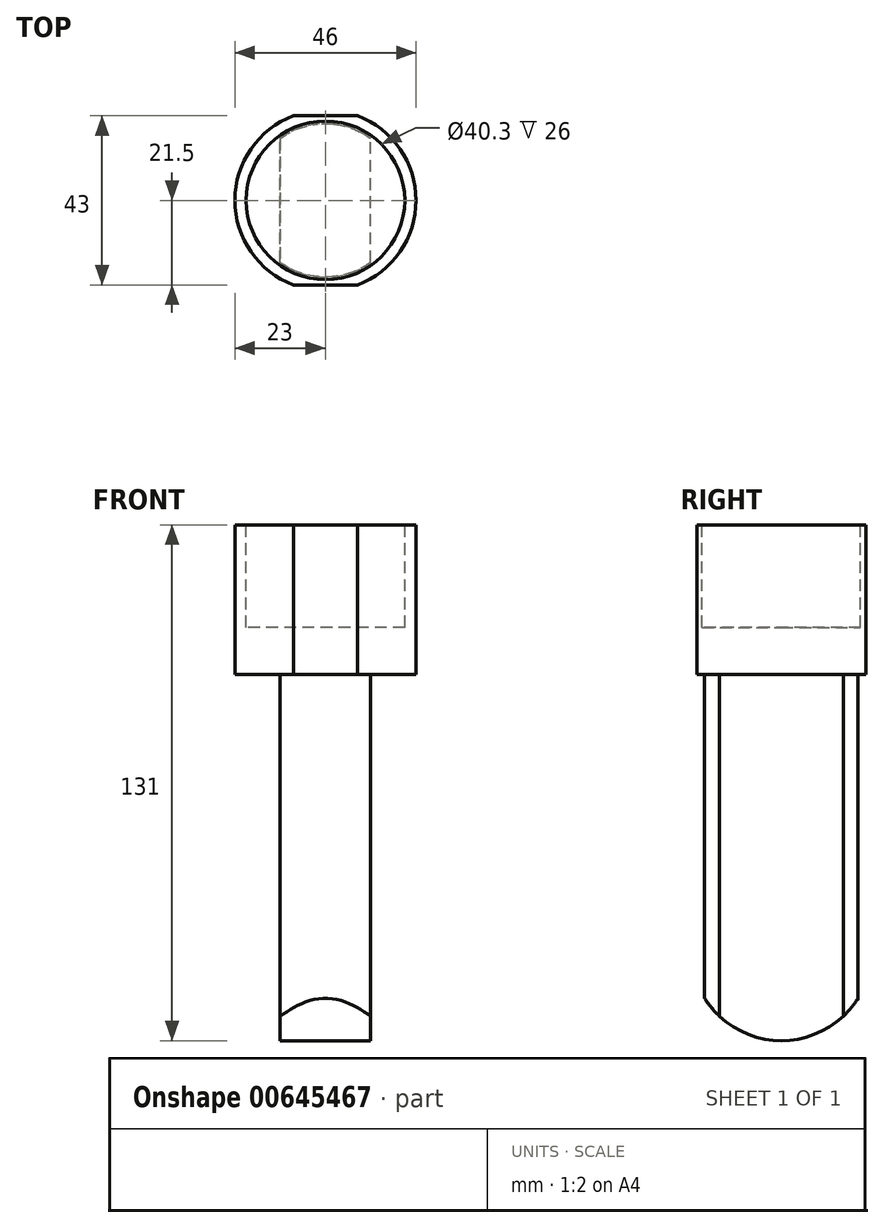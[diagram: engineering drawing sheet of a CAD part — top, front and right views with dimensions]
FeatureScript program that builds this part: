
annotation { "Feature Type Name" : "Feature", "Feature Type Description" : "" }
export const myFeature = defineFeature(function(context is Context, id is Id, definition is map)
    precondition{}
    {
        {
            var Q0;
            Q0=qCreatedBy(makeId("Top.planeOp"),FACE);
            var sketch = newSketch(context, id + "F0", { "sketchPlane" : qUnion([Q0])});
            skArc(sketch, "E0", {"start": v(8.17, -21.5) * mm, "mid": v(23, 0) * mm, "end": v(8.17, 21.5) * mm});
            skLineSegment(sketch, "E1", {"start": v(-8.17, -21.5) * mm, "end": v(8.17, -21.5) * mm});
            skLineSegment(sketch, "E2.MirrorCS", {"start": v(-8.17, 21.5) * mm, "end": v(8.17, 21.5) * mm});
            skArc(sketch, "E3.trimOffspring", {"start": v(-8.17, 21.5) * mm, "mid": v(-23, 0) * mm, "end": v(-8.17, -21.5) * mm});
            skSolve(sketch);
        }
        {
            var Q0;
            Q0 = qSketchRegion(id + "F0", true);
            extrude(context, id + "F1", {"entities" : qUnion([Q0]), "depth" : 38 * mm, "offsetDistance" : 25 * mm});
        }
        {
            var Q0;
            Q0=makeQuery(id+"F1.opExtrude","CAP_FACE",FACE,{"disambiguationData":[OSD([sQuery(id+"F0.wireOp",EDGE,"E0"),sQuery(id+"F0.wireOp",EDGE,"E1"),sQuery(id+"F0.wireOp",EDGE,"E2.MirrorCS"),sQuery(id+"F0.wireOp",EDGE,"E3.trimOffspring")])],"isStart":false});
            var sketch = newSketch(context, id + "F2", { "sketchPlane" : qUnion([Q0])});
            skCircle(sketch, "E4", {"center": v(0, 0) * mm, "radius": 20.15 * mm});
            skSolve(sketch);
        }
        {
            var Q0;
            Q0 = qSketchRegion(id + "F2", true);
            extrude(context, id + "F3", {"entities" : qUnion([Q0]), "operationType" : NewBodyOperationType.REMOVE, "oppositeDirection" : true, "depth" : 26 * mm, "offsetDistance" : 25 * mm});
        }
        {
            var Q0;
            Q0=makeQuery(id+"F1.opExtrude","CAP_FACE",FACE,{"disambiguationData":[OSD([sQuery(id+"F0.wireOp",EDGE,"E0"),sQuery(id+"F0.wireOp",EDGE,"E1"),sQuery(id+"F0.wireOp",EDGE,"E2.MirrorCS"),sQuery(id+"F0.wireOp",EDGE,"E3.trimOffspring")])],"isStart":true});
            var sketch = newSketch(context, id + "F4", { "sketchPlane" : qUnion([Q0])});
            skArc(sketch, "E5", {"start": v(-11.5, -15.75) * mm, "mid": v(0, -19.5) * mm, "end": v(11.5, -15.75) * mm});
            skLineSegment(sketch, "E6", {"start": v(-11.5, 15.75) * mm, "end": v(-11.5, -15.75) * mm});
            skLineSegment(sketch, "E7.MirrorCS", {"start": v(11.5, 15.75) * mm, "end": v(11.5, -15.75) * mm});
            skArc(sketch, "E8.trimOffspring", {"start": v(11.5, 15.75) * mm, "mid": v(0, 19.5) * mm, "end": v(-11.5, 15.75) * mm});
            skSolve(sketch);
        }
        {
            var Q0;
            Q0=makeQuery(id+"F4.imprint","IMPRINT",FACE,{"disambiguationData":[TD([[makeQuery(id+"F4.imprint","IMPRINT",EDGE,{"derivedFrom":sQuery(id+"F4.wireOp",EDGE,"E5")}),1.0]])]});
            extrude(context, id + "F5", {"entities" : qUnion([Q0]), "operationType" : NewBodyOperationType.ADD, "depth" : 93 * mm, "offsetDistance" : 25 * mm});
        }
        {
            var Q0;
            Q0=makeQuery(id+"F5.opExtrude","SWEPT_FACE",FACE,{"disambiguationData":[OSD([sQuery(id+"F4.wireOp",EDGE,"E6")])]});
            var sketch = newSketch(context, id + "F6", { "sketchPlane" : qUnion([Q0])});
            skCircle(sketch, "E9", {"center": v(0, -70) * mm, "radius": 23 * mm});
            skLineSegment(sketch, "E10", {"start": v(-19.4, -82.36) * mm, "end": v(-29.57, -99.34) * mm});
            skLineSegment(sketch, "E11", {"start": v(-29.57, -99.34) * mm, "end": v(32.34, -99.34) * mm});
            skLineSegment(sketch, "E12", {"start": v(32.34, -99.34) * mm, "end": v(19.7, -81.88) * mm});
            skSolve(sketch);
        }
        {
            var Q0;
            {var subQ5=sQuery(id+"F6.wireOp",EDGE,"E10");Q0=makeQuery(id+"F6.imprint","IMPRINT",FACE,{"disambiguationData":[TD([[makeQuery(id+"F6.imprint","IMPRINT",EDGE,{"derivedFrom":subQ5}),1.0]])]});}
            var Q1;
            {var subQ0=sQuery(id+"F6.wireOp",EDGE,"E9");var subQ1=sQuery(id+"F4.wireOp",EDGE,"E6");var subQ4=makeQuery(id+"F5.opExtrude","CAP_EDGE",EDGE,{"disambiguationData":[OSD([subQ1])],"isStart":false});var subQ5=makeQuery(id+"F6.imprint","INTERSECT",VERTEX,{"derivedFrom":[subQ4,subQ0]});Q1=makeQuery(id+"F6.imprint","IMPRINT",FACE,{"disambiguationData":[TD([[makeQuery(id+"F6.imprint","IMPRINT",EDGE,{"disambiguationData":[TD([[subQ5,1.0]])],"derivedFrom":subQ0}),-1.0]])]});}
            var Q2;
            {var subQ0=sQuery(id+"F6.wireOp",EDGE,"E9");var subQ1=sQuery(id+"F4.wireOp",EDGE,"E6");var subQ2=makeQuery(id+"F5.opExtrude","CAP_EDGE",EDGE,{"disambiguationData":[OSD([subQ1])],"isStart":false});var subQ3=makeQuery(id+"F6.imprint","INTERSECT",VERTEX,{"derivedFrom":[subQ2,subQ0]});Q2=makeQuery(id+"F6.imprint","IMPRINT",FACE,{"disambiguationData":[TD([[makeQuery(id+"F6.imprint","IMPRINT",EDGE,{"disambiguationData":[TD([[subQ3,-1.0]])],"derivedFrom":subQ0}),-1.0]])]});}
            extrude(context, id + "F7", {"entities" : qUnion([Q0, Q1, Q2]), "operationType" : NewBodyOperationType.REMOVE, "endBound" : BoundingType.THROUGH_ALL, "oppositeDirection" : true, "depth" : 25 * mm, "offsetDistance" : 25 * mm});
        }
    });
